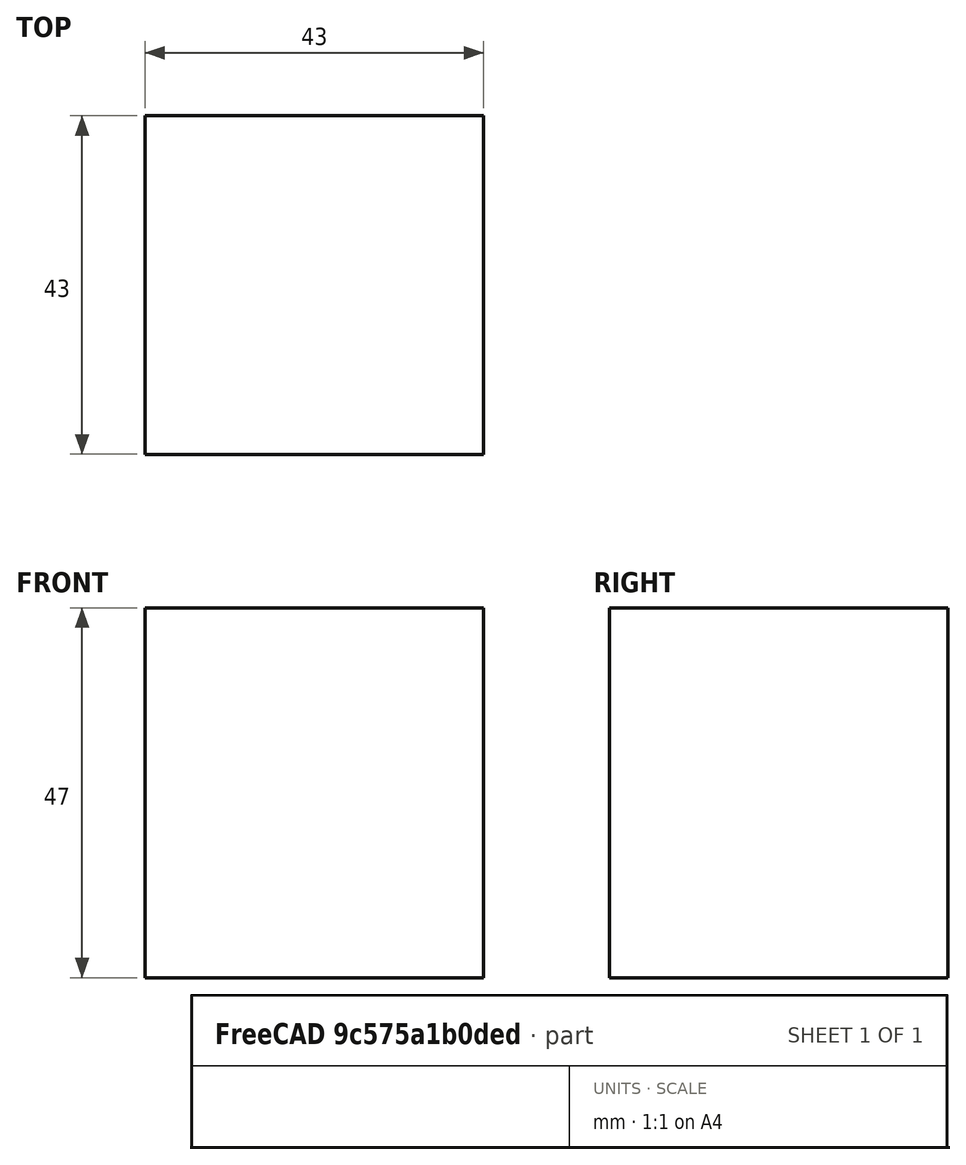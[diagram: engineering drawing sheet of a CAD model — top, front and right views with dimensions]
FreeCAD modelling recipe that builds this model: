
FCSTD DOCUMENT  (FreeCAD 0.18R16110 (Git))
Label: aaaaaa
License: All rights reserved
LicenseURL: http://en.wikipedia.org/wiki/All_rights_reserved
objects: Sketcher::SketchObject×2, Part::Extrusion×1
note: 3 computed .brp shape members not serialized (recipe doc carries the construction recipe); baked Part::Feature solids carry a one-line shape summary decoded from their .brp

FEATURE [Sketcher::SketchObject] Sketch
  sketch-geometry (4):
    g0: LineSegment StartX=-70.7793 StartY=41.0372 StartZ=0 EndX=-27.7793 EndY=41.0372 EndZ=0
    g1: LineSegment StartX=-27.7793 StartY=41.0372 StartZ=0 EndX=-27.7793 EndY=-1.96276 EndZ=0
    g2: LineSegment StartX=-27.7793 StartY=-1.96276 StartZ=0 EndX=-70.7793 EndY=-1.96276 EndZ=0
    g3: LineSegment StartX=-70.7793 StartY=-1.96276 StartZ=0 EndX=-70.7793 EndY=41.0372 EndZ=0
  constraints (8):
    c: Coincident(g0,g1)
    c: Coincident(g1,g2)
    c: Coincident(g2,g3)
    c: Coincident(g3,g0)
    c: Horizontal(g0)
    c: Horizontal(g2)
    c: Vertical(g1)
    c: Vertical(g3)
FEATURE [Part::Extrusion] Extrude
  Base = -> Sketch
  Dir = (0,0,1)
  DirMode = 2
  FaceMakerClass = Part::FaceMakerBullseye
  LengthFwd = 47
  LengthRev = 0
  Solid = true
  Symmetric = false
FEATURE [Sketcher::SketchObject] Sketch001
  sketch-geometry (23):
    g0: GeomPoint X=-70.7767 Y=41.0421 Z=0
    g1: GeomPoint X=-27.829 Y=41.033 Z=0
    g2: GeomPoint X=-70.7734 Y=-1.94844 Z=0
    g3: GeomPoint X=-27.7738 Y=-1.93663 Z=0
    g4: LineSegment StartX=-69.7767 StartY=40.033 StartZ=0 EndX=-28.829 EndY=40.033 EndZ=0
    g5: LineSegment StartX=-28.7738 StartY=-0.948438 StartZ=0 EndX=-69.7788 EndY=-0.948438 EndZ=0
    g6: LineSegment StartX=-28.7738 StartY=-0.948438 StartZ=0 EndX=-28.7738 EndY=16.4516 EndZ=0
    g7: GeomPoint X=-28.6402 Y=-0.958209 Z=0
    g8: LineSegment StartX=-69.7734 StartY=-0.945835 StartZ=0 EndX=-69.7734 EndY=16.4234 EndZ=0
    g9: LineSegment StartX=-28.8049 StartY=40.0503 StartZ=0 EndX=-28.8049 EndY=22.6503 EndZ=0
    g10: LineSegment StartX=-69.7767 StartY=40.0234 StartZ=0 EndX=-69.7767 EndY=22.6234 EndZ=0
    g11: LineSegment StartX=-69.6957 StartY=18.3565 StartZ=0 EndX=-69.6957 EndY=20.5034 EndZ=0
    g12: LineSegment StartX=-29.2049 StartY=20.5565 StartZ=0 EndX=-29.2049 EndY=18.3565 EndZ=0
    g13: LineSegment StartX=-28.8049 StartY=22.6503 StartZ=0 EndX=-30.5577 EndY=20.5034 EndZ=0
    g14: LineSegment StartX=-28.7915 StartY=16.4477 StartZ=0 EndX=-30.4263 EndY=18.28 EndZ=0
    g15: LineSegment StartX=-30.5769 StartY=20.48 StartZ=0 EndX=-29.2032 EndY=20.48 EndZ=0
    g16: LineSegment StartX=-29.2032 StartY=20.48 StartZ=0 EndX=-29.2032 EndY=18.3565 EndZ=0
    g17: LineSegment StartX=-29.2032 StartY=18.3565 StartZ=0 EndX=-30.4107 EndY=18.3565 EndZ=0
    g18: LineSegment StartX=-69.7965 StartY=16.4065 StartZ=0 EndX=-68.2824 EndY=18.3565 EndZ=0
    g19: LineSegment StartX=-68.2824 StartY=18.3565 StartZ=0 EndX=-69.721 EndY=18.3565 EndZ=0
    g20: LineSegment StartX=-69.721 StartY=18.3565 StartZ=0 EndX=-69.721 EndY=20.5565 EndZ=0
    g21: LineSegment StartX=-69.721 StartY=20.5565 StartZ=0 EndX=-68.0987 EndY=20.5565 EndZ=0
    g22: LineSegment StartX=-68.0987 StartY=20.5565 StartZ=0 EndX=-69.7808 EndY=22.6216 EndZ=0
  constraints (20):
    c: Horizontal(g4)
    c: Horizontal(g5)
    c: Coincident(g6,g5)
    c: Vertical(g6)
    c: Vertical(g8)
    c: Vertical(g9)
    c: Vertical(g10)
    c: Vertical(g11)
    c: Vertical(g12)
    c: PointOnObject(g15,g13)
    c: Horizontal(g15)
    c: Coincident(g15,g16)
    c: Vertical(g16)
    c: Coincident(g16,g17)
    c: Coincident(g18,g19)
    c: Coincident(g19,g20)
    c: Vertical(g20)
    c: Coincident(g20,g21)
    c: Horizontal(g21)
    c: Coincident(g21,g22)
